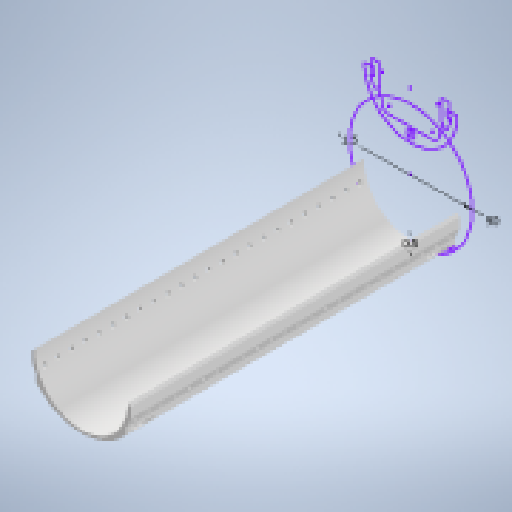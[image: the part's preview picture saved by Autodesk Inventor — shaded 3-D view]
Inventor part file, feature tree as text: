
AUTODESK INVENTOR PART (.ipt)
format: ipt  version: 2023 (Build 270158030, 158C)  size: 393,216 bytes
history: native  units: in
note: dims shown in document units (in); Inventor stores cm internally (conversion verified against a paired STEP export)
features: sketch x10, extrude x3, sweep x2, projected_geometry x2
ambient origin geometry x8: Origin, YZ Plane, XZ Plane, XY Plane, X Axis, Y Axis, Z Axis, Center Point
bodies: Solid1 (feature_tree)
feature tree (17):
  sketch  "Sketch1"  dims[d0=3.5433in d2=0.0591in d3=0.0197in d6=0.0in]
  sketch  "Sketch2"  dims[d7=1.7554in d8=0.3463in]
  extrude  "Extrusion1"  Depth=0.0in
  sketch  "Sketch5"  dims[d11=1.2598in d12=-1.0187in]
  extrude  "Extrusion2"  Depth=0.3463in
  extrude  "Extrusion3"  Depth=0.1772in
  sweep  "Sweep1"
  sweep  "Sweep2"
  sketch  "Sketch11"  dims[d19=2.6772in d20=1.3386in d21=0.3078in d22=0.3078in d23=0.1832in d24=0.1832in d25=0.1484in d26=0.1484in d27=0.7916in d28=0.7916in d29=0.2913in d30=90.0deg d31=90.0deg d32=0.126in d33=90.0deg d34=0.126in d35=90.0deg d36=0.2707in d37=90.0deg d38=0.2707in d39=90.0deg d40=0.0787in d43=0.1969in d49=0.1969in d50=1.2297in d51=1.2525in d52=0.0984in d54=0.0984in d55=9.4488in d56=0.0in d66=0.1181in d67=0.1969in d68=9.4488in d70=0.3937in d71=0.3937in d73=0.3937in d75=0.1181in d76=0.1969in d77=9.4488in d79=0.3937in d80=0.3937in d82=0.3937in d84=0.3937in d85=0.0in d86=0.3937in d87=0.0in d88=0.5906in d89=0.0394in d90=0.0394in d91=0.1969in d92=1.6535in d93=0.0in d94=0.0in d95=0.5906in d96=180.0deg d97=0.0394in d98=0.1969in d99=0.0394in d100=1.6535in d101=0.0in d102=0.0in d103=0.315in d104=1.0236in d105=1.0236in d106=1.3386in]
  sketch  "Sketch3"  dims[d9=0.1772in d10=0.1772in]
  projected_geometry  "Projected Loop1"
  sketch  "Sketch6"  dims[d13=2.0615in d14=2.6772in]
  projected_geometry  "Projected Loop2"
  sketch  "Sketch7"  dims[d15=1.2368in]
  sketch  "Sketch8"  dims[d16=-1.1959in]
  sketch  "Sketch9"  dims[d17=0.8835in]
  sketch  "Sketch10"  dims[d18=1.3444in]
